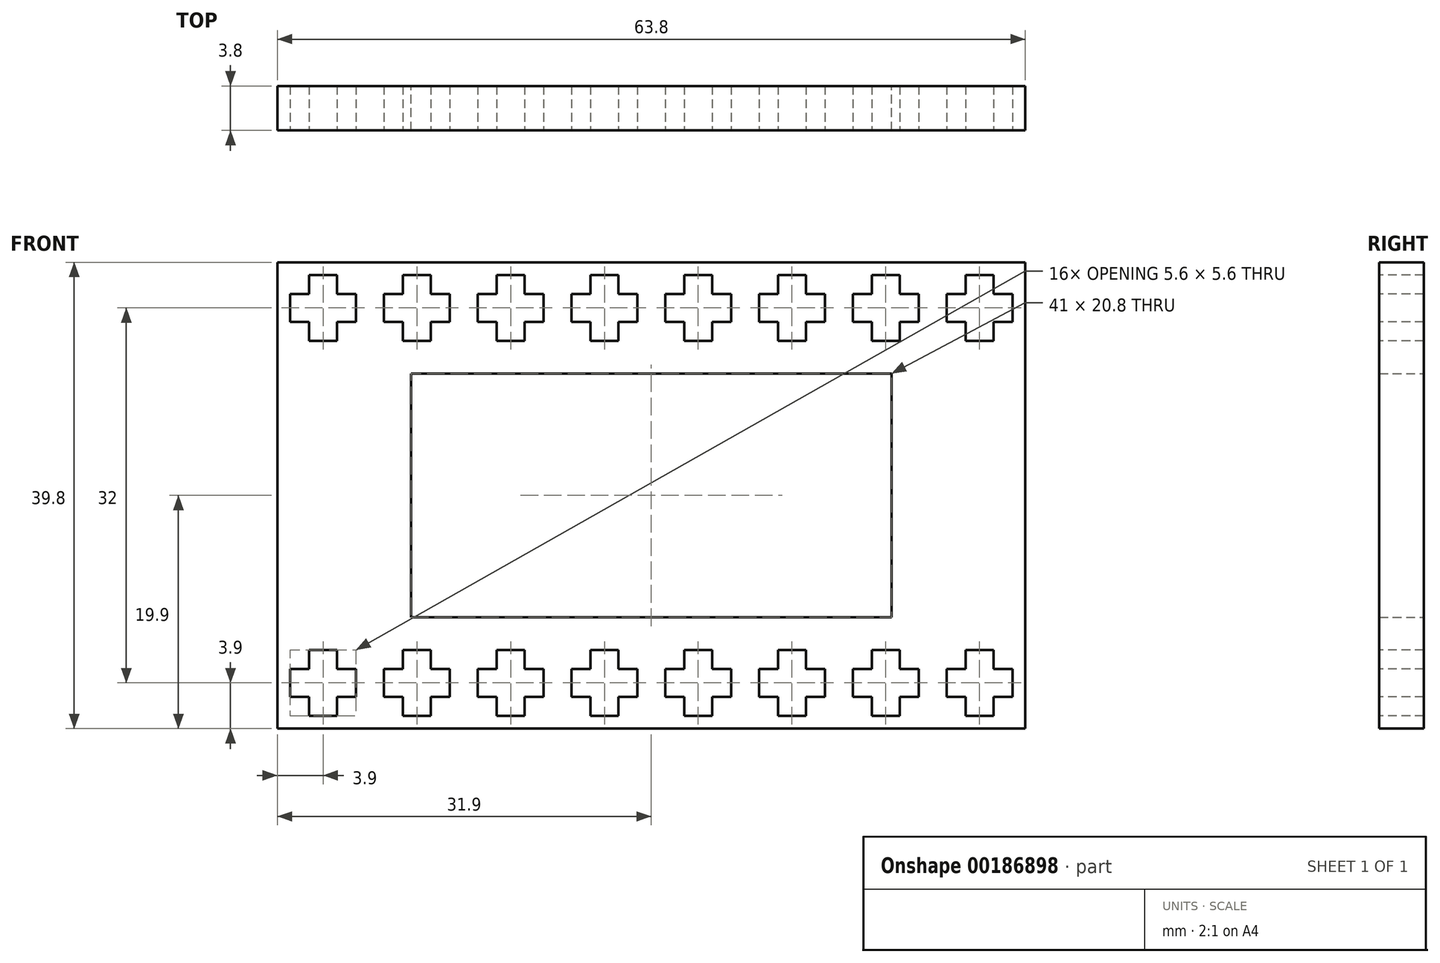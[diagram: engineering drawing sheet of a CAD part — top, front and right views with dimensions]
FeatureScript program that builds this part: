
annotation { "Feature Type Name" : "Feature", "Feature Type Description" : "" }
export const myFeature = defineFeature(function(context is Context, id is Id, definition is map)
    precondition{}
    {
        {
            var Q0;
            Q0=qCreatedBy(makeId("Front.planeOp"),FACE);
            var sketch = newSketch(context, id + "F0", { "sketchPlane" : qUnion([Q0])});
            skLineSegment(sketch, "E0.bottom", {"start": v(20.5, 10.4) * mm, "end": v(-20.5, 10.4) * mm});
            skLineSegment(sketch, "E0.top", {"start": v(20.5, -10.4) * mm, "end": v(-20.5, -10.4) * mm});
            skLineSegment(sketch, "E0.left", {"start": v(20.5, 10.4) * mm, "end": v(20.5, -10.4) * mm});
            skLineSegment(sketch, "E0.right", {"start": v(-20.5, 10.4) * mm, "end": v(-20.5, -10.4) * mm});
            skPoint(sketch, "E0.middle", {"position": v(0, 0) * mm});
            skLineSegment(sketch, "E1.bottom", {"start": v(31.9, -19.9) * mm, "end": v(-31.9, -19.9) * mm});
            skLineSegment(sketch, "E1.top", {"start": v(31.9, 19.9) * mm, "end": v(-31.9, 19.9) * mm});
            skLineSegment(sketch, "E1.left", {"start": v(31.9, -19.9) * mm, "end": v(31.9, 19.9) * mm});
            skLineSegment(sketch, "E1.right", {"start": v(-31.9, -19.9) * mm, "end": v(-31.9, 19.9) * mm});
            skSolve(sketch);
        }
        {
            var Q0;
            Q0 = qSketchRegion(id + "F0", true);
            extrude(context, id + "F1", {"entities" : qUnion([Q0]), "depth" : 3.8 * mm});
        }
        {
            var Q0;
            Q0=makeQuery(id+"F1.opExtrude","CAP_FACE",FACE,{"disambiguationData":[OSD([sQuery(id+"F0.wireOp",EDGE,"E0.bottom"),sQuery(id+"F0.wireOp",EDGE,"E0.top"),sQuery(id+"F0.wireOp",EDGE,"E0.left"),sQuery(id+"F0.wireOp",EDGE,"E0.right"),sQuery(id+"F0.wireOp",EDGE,"E1.bottom"),sQuery(id+"F0.wireOp",EDGE,"E1.top"),sQuery(id+"F0.wireOp",EDGE,"E1.left"),sQuery(id+"F0.wireOp",EDGE,"E1.right")])],"isStart":false});
            var sketch = newSketch(context, id + "F2", { "sketchPlane" : qUnion([Q0])});
            skLineSegment(sketch, "E2", {"start": v(-30.8, 17.2) * mm, "end": v(-29.2, 17.2) * mm});
            skLineSegment(sketch, "E3", {"start": v(-29.2, 17.2) * mm, "end": v(-29.2, 18.8) * mm});
            skLineSegment(sketch, "E4", {"start": v(-29.2, 18.8) * mm, "end": v(-26.8, 18.8) * mm});
            skLineSegment(sketch, "E5", {"start": v(-26.8, 18.8) * mm, "end": v(-26.8, 17.2) * mm});
            skLineSegment(sketch, "E6", {"start": v(-26.8, 17.2) * mm, "end": v(-25.2, 17.2) * mm});
            skLineSegment(sketch, "E7", {"start": v(-25.2, 17.2) * mm, "end": v(-25.2, 14.8) * mm});
            skLineSegment(sketch, "E8", {"start": v(-25.2, 14.8) * mm, "end": v(-26.8, 14.8) * mm});
            skLineSegment(sketch, "E9", {"start": v(-26.8, 14.8) * mm, "end": v(-26.8, 13.2) * mm});
            skLineSegment(sketch, "E10", {"start": v(-26.8, 13.2) * mm, "end": v(-29.2, 13.2) * mm});
            skLineSegment(sketch, "E11", {"start": v(-29.2, 13.2) * mm, "end": v(-29.2, 14.8) * mm});
            skLineSegment(sketch, "E12", {"start": v(-30.8, 17.2) * mm, "end": v(-30.8, 14.8) * mm});
            skLineSegment(sketch, "E13", {"start": v(-30.8, 14.8) * mm, "end": v(-29.2, 14.8) * mm});
            skPoint(sketch, "E14", {"position": v(-30.8, 16) * mm});
            skPoint(sketch, "E15", {"position": v(-28, 18.8) * mm});
            skLineSegment(sketch, "E16.0.1.0", {"start": v(-29.2, -13.2) * mm, "end": v(-26.8, -13.2) * mm});
            skLineSegment(sketch, "E16.0.1.1", {"start": v(-26.8, -13.2) * mm, "end": v(-26.8, -14.8) * mm});
            skLineSegment(sketch, "E16.0.1.2", {"start": v(-26.8, -14.8) * mm, "end": v(-25.2, -14.8) * mm});
            skLineSegment(sketch, "E16.0.1.3", {"start": v(-25.2, -14.8) * mm, "end": v(-25.2, -17.2) * mm});
            skLineSegment(sketch, "E16.0.1.4", {"start": v(-25.2, -17.2) * mm, "end": v(-26.8, -17.2) * mm});
            skLineSegment(sketch, "E16.0.1.5", {"start": v(-26.8, -17.2) * mm, "end": v(-26.8, -18.8) * mm});
            skLineSegment(sketch, "E16.0.1.6", {"start": v(-29.2, -18.8) * mm, "end": v(-29.2, -17.2) * mm});
            skLineSegment(sketch, "E16.0.1.7", {"start": v(-30.8, -17.2) * mm, "end": v(-29.2, -17.2) * mm});
            skLineSegment(sketch, "E16.0.1.8", {"start": v(-30.8, -14.8) * mm, "end": v(-30.8, -17.2) * mm});
            skLineSegment(sketch, "E16.0.1.9", {"start": v(-30.8, -14.8) * mm, "end": v(-29.2, -14.8) * mm});
            skLineSegment(sketch, "E16.0.1.10", {"start": v(-29.2, -14.8) * mm, "end": v(-29.2, -13.2) * mm});
            skLineSegment(sketch, "E16.0.1.11", {"start": v(-26.8, -18.8) * mm, "end": v(-29.2, -18.8) * mm});
            skLineSegment(sketch, "E16.1.0.0", {"start": v(-21.2, 18.8) * mm, "end": v(-18.8, 18.8) * mm});
            skLineSegment(sketch, "E16.1.0.1", {"start": v(-18.8, 18.8) * mm, "end": v(-18.8, 17.2) * mm});
            skLineSegment(sketch, "E16.1.0.2", {"start": v(-18.8, 17.2) * mm, "end": v(-17.2, 17.2) * mm});
            skLineSegment(sketch, "E16.1.0.3", {"start": v(-17.2, 17.2) * mm, "end": v(-17.2, 14.8) * mm});
            skLineSegment(sketch, "E16.1.0.4", {"start": v(-17.2, 14.8) * mm, "end": v(-18.8, 14.8) * mm});
            skLineSegment(sketch, "E16.1.0.5", {"start": v(-18.8, 14.8) * mm, "end": v(-18.8, 13.2) * mm});
            skLineSegment(sketch, "E16.1.0.6", {"start": v(-21.2, 13.2) * mm, "end": v(-21.2, 14.8) * mm});
            skLineSegment(sketch, "E16.1.0.7", {"start": v(-22.8, 14.8) * mm, "end": v(-21.2, 14.8) * mm});
            skLineSegment(sketch, "E16.1.0.8", {"start": v(-22.8, 17.2) * mm, "end": v(-22.8, 14.8) * mm});
            skLineSegment(sketch, "E16.1.0.9", {"start": v(-22.8, 17.2) * mm, "end": v(-21.2, 17.2) * mm});
            skLineSegment(sketch, "E16.1.0.10", {"start": v(-21.2, 17.2) * mm, "end": v(-21.2, 18.8) * mm});
            skLineSegment(sketch, "E16.1.0.11", {"start": v(-18.8, 13.2) * mm, "end": v(-21.2, 13.2) * mm});
            skLineSegment(sketch, "E16.1.1.0", {"start": v(-21.2, -13.2) * mm, "end": v(-18.8, -13.2) * mm});
            skLineSegment(sketch, "E16.1.1.1", {"start": v(-18.8, -13.2) * mm, "end": v(-18.8, -14.8) * mm});
            skLineSegment(sketch, "E16.1.1.2", {"start": v(-18.8, -14.8) * mm, "end": v(-17.2, -14.8) * mm});
            skLineSegment(sketch, "E16.1.1.3", {"start": v(-17.2, -14.8) * mm, "end": v(-17.2, -17.2) * mm});
            skLineSegment(sketch, "E16.1.1.4", {"start": v(-17.2, -17.2) * mm, "end": v(-18.8, -17.2) * mm});
            skLineSegment(sketch, "E16.1.1.5", {"start": v(-18.8, -17.2) * mm, "end": v(-18.8, -18.8) * mm});
            skLineSegment(sketch, "E16.1.1.6", {"start": v(-21.2, -18.8) * mm, "end": v(-21.2, -17.2) * mm});
            skLineSegment(sketch, "E16.1.1.7", {"start": v(-22.8, -17.2) * mm, "end": v(-21.2, -17.2) * mm});
            skLineSegment(sketch, "E16.1.1.8", {"start": v(-22.8, -14.8) * mm, "end": v(-22.8, -17.2) * mm});
            skLineSegment(sketch, "E16.1.1.9", {"start": v(-22.8, -14.8) * mm, "end": v(-21.2, -14.8) * mm});
            skLineSegment(sketch, "E16.1.1.10", {"start": v(-21.2, -14.8) * mm, "end": v(-21.2, -13.2) * mm});
            skLineSegment(sketch, "E16.1.1.11", {"start": v(-18.8, -18.8) * mm, "end": v(-21.2, -18.8) * mm});
            skLineSegment(sketch, "E16.2.0.0", {"start": v(-13.2, 18.8) * mm, "end": v(-10.8, 18.8) * mm});
            skLineSegment(sketch, "E16.2.0.1", {"start": v(-10.8, 18.8) * mm, "end": v(-10.8, 17.2) * mm});
            skLineSegment(sketch, "E16.2.0.2", {"start": v(-10.8, 17.2) * mm, "end": v(-9.2, 17.2) * mm});
            skLineSegment(sketch, "E16.2.0.3", {"start": v(-9.2, 17.2) * mm, "end": v(-9.2, 14.8) * mm});
            skLineSegment(sketch, "E16.2.0.4", {"start": v(-9.2, 14.8) * mm, "end": v(-10.8, 14.8) * mm});
            skLineSegment(sketch, "E16.2.0.5", {"start": v(-10.8, 14.8) * mm, "end": v(-10.8, 13.2) * mm});
            skLineSegment(sketch, "E16.2.0.6", {"start": v(-13.2, 13.2) * mm, "end": v(-13.2, 14.8) * mm});
            skLineSegment(sketch, "E16.2.0.7", {"start": v(-14.8, 14.8) * mm, "end": v(-13.2, 14.8) * mm});
            skLineSegment(sketch, "E16.2.0.8", {"start": v(-14.8, 17.2) * mm, "end": v(-14.8, 14.8) * mm});
            skLineSegment(sketch, "E16.2.0.9", {"start": v(-14.8, 17.2) * mm, "end": v(-13.2, 17.2) * mm});
            skLineSegment(sketch, "E16.2.0.10", {"start": v(-13.2, 17.2) * mm, "end": v(-13.2, 18.8) * mm});
            skLineSegment(sketch, "E16.2.0.11", {"start": v(-10.8, 13.2) * mm, "end": v(-13.2, 13.2) * mm});
            skLineSegment(sketch, "E16.2.1.0", {"start": v(-13.2, -13.2) * mm, "end": v(-10.8, -13.2) * mm});
            skLineSegment(sketch, "E16.2.1.1", {"start": v(-10.8, -13.2) * mm, "end": v(-10.8, -14.8) * mm});
            skLineSegment(sketch, "E16.2.1.2", {"start": v(-10.8, -14.8) * mm, "end": v(-9.2, -14.8) * mm});
            skLineSegment(sketch, "E16.2.1.3", {"start": v(-9.2, -14.8) * mm, "end": v(-9.2, -17.2) * mm});
            skLineSegment(sketch, "E16.2.1.4", {"start": v(-9.2, -17.2) * mm, "end": v(-10.8, -17.2) * mm});
            skLineSegment(sketch, "E16.2.1.5", {"start": v(-10.8, -17.2) * mm, "end": v(-10.8, -18.8) * mm});
            skLineSegment(sketch, "E16.2.1.6", {"start": v(-13.2, -18.8) * mm, "end": v(-13.2, -17.2) * mm});
            skLineSegment(sketch, "E16.2.1.7", {"start": v(-14.8, -17.2) * mm, "end": v(-13.2, -17.2) * mm});
            skLineSegment(sketch, "E16.2.1.8", {"start": v(-14.8, -14.8) * mm, "end": v(-14.8, -17.2) * mm});
            skLineSegment(sketch, "E16.2.1.9", {"start": v(-14.8, -14.8) * mm, "end": v(-13.2, -14.8) * mm});
            skLineSegment(sketch, "E16.2.1.10", {"start": v(-13.2, -14.8) * mm, "end": v(-13.2, -13.2) * mm});
            skLineSegment(sketch, "E16.2.1.11", {"start": v(-10.8, -18.8) * mm, "end": v(-13.2, -18.8) * mm});
            skLineSegment(sketch, "E16.3.0.0", {"start": v(-5.2, 18.8) * mm, "end": v(-2.8, 18.8) * mm});
            skLineSegment(sketch, "E16.3.0.1", {"start": v(-2.8, 18.8) * mm, "end": v(-2.8, 17.2) * mm});
            skLineSegment(sketch, "E16.3.0.2", {"start": v(-2.8, 17.2) * mm, "end": v(-1.2, 17.2) * mm});
            skLineSegment(sketch, "E16.3.0.3", {"start": v(-1.2, 17.2) * mm, "end": v(-1.2, 14.8) * mm});
            skLineSegment(sketch, "E16.3.0.4", {"start": v(-1.2, 14.8) * mm, "end": v(-2.8, 14.8) * mm});
            skLineSegment(sketch, "E16.3.0.5", {"start": v(-2.8, 14.8) * mm, "end": v(-2.8, 13.2) * mm});
            skLineSegment(sketch, "E16.3.0.6", {"start": v(-5.2, 13.2) * mm, "end": v(-5.2, 14.8) * mm});
            skLineSegment(sketch, "E16.3.0.7", {"start": v(-6.8, 14.8) * mm, "end": v(-5.2, 14.8) * mm});
            skLineSegment(sketch, "E16.3.0.8", {"start": v(-6.8, 17.2) * mm, "end": v(-6.8, 14.8) * mm});
            skLineSegment(sketch, "E16.3.0.9", {"start": v(-6.8, 17.2) * mm, "end": v(-5.2, 17.2) * mm});
            skLineSegment(sketch, "E16.3.0.10", {"start": v(-5.2, 17.2) * mm, "end": v(-5.2, 18.8) * mm});
            skLineSegment(sketch, "E16.3.0.11", {"start": v(-2.8, 13.2) * mm, "end": v(-5.2, 13.2) * mm});
            skLineSegment(sketch, "E16.3.1.0", {"start": v(-5.2, -13.2) * mm, "end": v(-2.8, -13.2) * mm});
            skLineSegment(sketch, "E16.3.1.1", {"start": v(-2.8, -13.2) * mm, "end": v(-2.8, -14.8) * mm});
            skLineSegment(sketch, "E16.3.1.2", {"start": v(-2.8, -14.8) * mm, "end": v(-1.2, -14.8) * mm});
            skLineSegment(sketch, "E16.3.1.3", {"start": v(-1.2, -14.8) * mm, "end": v(-1.2, -17.2) * mm});
            skLineSegment(sketch, "E16.3.1.4", {"start": v(-1.2, -17.2) * mm, "end": v(-2.8, -17.2) * mm});
            skLineSegment(sketch, "E16.3.1.5", {"start": v(-2.8, -17.2) * mm, "end": v(-2.8, -18.8) * mm});
            skLineSegment(sketch, "E16.3.1.6", {"start": v(-5.2, -18.8) * mm, "end": v(-5.2, -17.2) * mm});
            skLineSegment(sketch, "E16.3.1.7", {"start": v(-6.8, -17.2) * mm, "end": v(-5.2, -17.2) * mm});
            skLineSegment(sketch, "E16.3.1.8", {"start": v(-6.8, -14.8) * mm, "end": v(-6.8, -17.2) * mm});
            skLineSegment(sketch, "E16.3.1.9", {"start": v(-6.8, -14.8) * mm, "end": v(-5.2, -14.8) * mm});
            skLineSegment(sketch, "E16.3.1.10", {"start": v(-5.2, -14.8) * mm, "end": v(-5.2, -13.2) * mm});
            skLineSegment(sketch, "E16.3.1.11", {"start": v(-2.8, -18.8) * mm, "end": v(-5.2, -18.8) * mm});
            skLineSegment(sketch, "E16.4.0.0", {"start": v(2.8, 18.8) * mm, "end": v(5.2, 18.8) * mm});
            skLineSegment(sketch, "E16.4.0.1", {"start": v(5.2, 18.8) * mm, "end": v(5.2, 17.2) * mm});
            skLineSegment(sketch, "E16.4.0.2", {"start": v(5.2, 17.2) * mm, "end": v(6.8, 17.2) * mm});
            skLineSegment(sketch, "E16.4.0.3", {"start": v(6.8, 17.2) * mm, "end": v(6.8, 14.8) * mm});
            skLineSegment(sketch, "E16.4.0.4", {"start": v(6.8, 14.8) * mm, "end": v(5.2, 14.8) * mm});
            skLineSegment(sketch, "E16.4.0.5", {"start": v(5.2, 14.8) * mm, "end": v(5.2, 13.2) * mm});
            skLineSegment(sketch, "E16.4.0.6", {"start": v(2.8, 13.2) * mm, "end": v(2.8, 14.8) * mm});
            skLineSegment(sketch, "E16.4.0.7", {"start": v(1.2, 14.8) * mm, "end": v(2.8, 14.8) * mm});
            skLineSegment(sketch, "E16.4.0.8", {"start": v(1.2, 17.2) * mm, "end": v(1.2, 14.8) * mm});
            skLineSegment(sketch, "E16.4.0.9", {"start": v(1.2, 17.2) * mm, "end": v(2.8, 17.2) * mm});
            skLineSegment(sketch, "E16.4.0.10", {"start": v(2.8, 17.2) * mm, "end": v(2.8, 18.8) * mm});
            skLineSegment(sketch, "E16.4.0.11", {"start": v(5.2, 13.2) * mm, "end": v(2.8, 13.2) * mm});
            skLineSegment(sketch, "E16.4.1.0", {"start": v(2.8, -13.2) * mm, "end": v(5.2, -13.2) * mm});
            skLineSegment(sketch, "E16.4.1.1", {"start": v(5.2, -13.2) * mm, "end": v(5.2, -14.8) * mm});
            skLineSegment(sketch, "E16.4.1.2", {"start": v(5.2, -14.8) * mm, "end": v(6.8, -14.8) * mm});
            skLineSegment(sketch, "E16.4.1.3", {"start": v(6.8, -14.8) * mm, "end": v(6.8, -17.2) * mm});
            skLineSegment(sketch, "E16.4.1.4", {"start": v(6.8, -17.2) * mm, "end": v(5.2, -17.2) * mm});
            skLineSegment(sketch, "E16.4.1.5", {"start": v(5.2, -17.2) * mm, "end": v(5.2, -18.8) * mm});
            skLineSegment(sketch, "E16.4.1.6", {"start": v(2.8, -18.8) * mm, "end": v(2.8, -17.2) * mm});
            skLineSegment(sketch, "E16.4.1.7", {"start": v(1.2, -17.2) * mm, "end": v(2.8, -17.2) * mm});
            skLineSegment(sketch, "E16.4.1.8", {"start": v(1.2, -14.8) * mm, "end": v(1.2, -17.2) * mm});
            skLineSegment(sketch, "E16.4.1.9", {"start": v(1.2, -14.8) * mm, "end": v(2.8, -14.8) * mm});
            skLineSegment(sketch, "E16.4.1.10", {"start": v(2.8, -14.8) * mm, "end": v(2.8, -13.2) * mm});
            skLineSegment(sketch, "E16.4.1.11", {"start": v(5.2, -18.8) * mm, "end": v(2.8, -18.8) * mm});
            skLineSegment(sketch, "E16.5.0.0", {"start": v(10.8, 18.8) * mm, "end": v(13.2, 18.8) * mm});
            skLineSegment(sketch, "E16.5.0.1", {"start": v(13.2, 18.8) * mm, "end": v(13.2, 17.2) * mm});
            skLineSegment(sketch, "E16.5.0.2", {"start": v(13.2, 17.2) * mm, "end": v(14.8, 17.2) * mm});
            skLineSegment(sketch, "E16.5.0.3", {"start": v(14.8, 17.2) * mm, "end": v(14.8, 14.8) * mm});
            skLineSegment(sketch, "E16.5.0.4", {"start": v(14.8, 14.8) * mm, "end": v(13.2, 14.8) * mm});
            skLineSegment(sketch, "E16.5.0.5", {"start": v(13.2, 14.8) * mm, "end": v(13.2, 13.2) * mm});
            skLineSegment(sketch, "E16.5.0.6", {"start": v(10.8, 13.2) * mm, "end": v(10.8, 14.8) * mm});
            skLineSegment(sketch, "E16.5.0.7", {"start": v(9.2, 14.8) * mm, "end": v(10.8, 14.8) * mm});
            skLineSegment(sketch, "E16.5.0.8", {"start": v(9.2, 17.2) * mm, "end": v(9.2, 14.8) * mm});
            skLineSegment(sketch, "E16.5.0.9", {"start": v(9.2, 17.2) * mm, "end": v(10.8, 17.2) * mm});
            skLineSegment(sketch, "E16.5.0.10", {"start": v(10.8, 17.2) * mm, "end": v(10.8, 18.8) * mm});
            skLineSegment(sketch, "E16.5.0.11", {"start": v(13.2, 13.2) * mm, "end": v(10.8, 13.2) * mm});
            skLineSegment(sketch, "E16.5.1.0", {"start": v(10.8, -13.2) * mm, "end": v(13.2, -13.2) * mm});
            skLineSegment(sketch, "E16.5.1.1", {"start": v(13.2, -13.2) * mm, "end": v(13.2, -14.8) * mm});
            skLineSegment(sketch, "E16.5.1.2", {"start": v(13.2, -14.8) * mm, "end": v(14.8, -14.8) * mm});
            skLineSegment(sketch, "E16.5.1.3", {"start": v(14.8, -14.8) * mm, "end": v(14.8, -17.2) * mm});
            skLineSegment(sketch, "E16.5.1.4", {"start": v(14.8, -17.2) * mm, "end": v(13.2, -17.2) * mm});
            skLineSegment(sketch, "E16.5.1.5", {"start": v(13.2, -17.2) * mm, "end": v(13.2, -18.8) * mm});
            skLineSegment(sketch, "E16.5.1.6", {"start": v(10.8, -18.8) * mm, "end": v(10.8, -17.2) * mm});
            skLineSegment(sketch, "E16.5.1.7", {"start": v(9.2, -17.2) * mm, "end": v(10.8, -17.2) * mm});
            skLineSegment(sketch, "E16.5.1.8", {"start": v(9.2, -14.8) * mm, "end": v(9.2, -17.2) * mm});
            skLineSegment(sketch, "E16.5.1.9", {"start": v(9.2, -14.8) * mm, "end": v(10.8, -14.8) * mm});
            skLineSegment(sketch, "E16.5.1.10", {"start": v(10.8, -14.8) * mm, "end": v(10.8, -13.2) * mm});
            skLineSegment(sketch, "E16.5.1.11", {"start": v(13.2, -18.8) * mm, "end": v(10.8, -18.8) * mm});
            skLineSegment(sketch, "E16.6.0.0", {"start": v(18.8, 18.8) * mm, "end": v(21.2, 18.8) * mm});
            skLineSegment(sketch, "E16.6.0.1", {"start": v(21.2, 18.8) * mm, "end": v(21.2, 17.2) * mm});
            skLineSegment(sketch, "E16.6.0.2", {"start": v(21.2, 17.2) * mm, "end": v(22.8, 17.2) * mm});
            skLineSegment(sketch, "E16.6.0.3", {"start": v(22.8, 17.2) * mm, "end": v(22.8, 14.8) * mm});
            skLineSegment(sketch, "E16.6.0.4", {"start": v(22.8, 14.8) * mm, "end": v(21.2, 14.8) * mm});
            skLineSegment(sketch, "E16.6.0.5", {"start": v(21.2, 14.8) * mm, "end": v(21.2, 13.2) * mm});
            skLineSegment(sketch, "E16.6.0.6", {"start": v(18.8, 13.2) * mm, "end": v(18.8, 14.8) * mm});
            skLineSegment(sketch, "E16.6.0.7", {"start": v(17.2, 14.8) * mm, "end": v(18.8, 14.8) * mm});
            skLineSegment(sketch, "E16.6.0.8", {"start": v(17.2, 17.2) * mm, "end": v(17.2, 14.8) * mm});
            skLineSegment(sketch, "E16.6.0.9", {"start": v(17.2, 17.2) * mm, "end": v(18.8, 17.2) * mm});
            skLineSegment(sketch, "E16.6.0.10", {"start": v(18.8, 17.2) * mm, "end": v(18.8, 18.8) * mm});
            skLineSegment(sketch, "E16.6.0.11", {"start": v(21.2, 13.2) * mm, "end": v(18.8, 13.2) * mm});
            skLineSegment(sketch, "E16.6.1.0", {"start": v(18.8, -13.2) * mm, "end": v(21.2, -13.2) * mm});
            skLineSegment(sketch, "E16.6.1.1", {"start": v(21.2, -13.2) * mm, "end": v(21.2, -14.8) * mm});
            skLineSegment(sketch, "E16.6.1.2", {"start": v(21.2, -14.8) * mm, "end": v(22.8, -14.8) * mm});
            skLineSegment(sketch, "E16.6.1.3", {"start": v(22.8, -14.8) * mm, "end": v(22.8, -17.2) * mm});
            skLineSegment(sketch, "E16.6.1.4", {"start": v(22.8, -17.2) * mm, "end": v(21.2, -17.2) * mm});
            skLineSegment(sketch, "E16.6.1.5", {"start": v(21.2, -17.2) * mm, "end": v(21.2, -18.8) * mm});
            skLineSegment(sketch, "E16.6.1.6", {"start": v(18.8, -18.8) * mm, "end": v(18.8, -17.2) * mm});
            skLineSegment(sketch, "E16.6.1.7", {"start": v(17.2, -17.2) * mm, "end": v(18.8, -17.2) * mm});
            skLineSegment(sketch, "E16.6.1.8", {"start": v(17.2, -14.8) * mm, "end": v(17.2, -17.2) * mm});
            skLineSegment(sketch, "E16.6.1.9", {"start": v(17.2, -14.8) * mm, "end": v(18.8, -14.8) * mm});
            skLineSegment(sketch, "E16.6.1.10", {"start": v(18.8, -14.8) * mm, "end": v(18.8, -13.2) * mm});
            skLineSegment(sketch, "E16.6.1.11", {"start": v(21.2, -18.8) * mm, "end": v(18.8, -18.8) * mm});
            skLineSegment(sketch, "E16.7.0.0", {"start": v(26.8, 18.8) * mm, "end": v(29.2, 18.8) * mm});
            skLineSegment(sketch, "E16.7.0.1", {"start": v(29.2, 18.8) * mm, "end": v(29.2, 17.2) * mm});
            skLineSegment(sketch, "E16.7.0.2", {"start": v(29.2, 17.2) * mm, "end": v(30.8, 17.2) * mm});
            skLineSegment(sketch, "E16.7.0.3", {"start": v(30.8, 17.2) * mm, "end": v(30.8, 14.8) * mm});
            skLineSegment(sketch, "E16.7.0.4", {"start": v(30.8, 14.8) * mm, "end": v(29.2, 14.8) * mm});
            skLineSegment(sketch, "E16.7.0.5", {"start": v(29.2, 14.8) * mm, "end": v(29.2, 13.2) * mm});
            skLineSegment(sketch, "E16.7.0.6", {"start": v(26.8, 13.2) * mm, "end": v(26.8, 14.8) * mm});
            skLineSegment(sketch, "E16.7.0.7", {"start": v(25.2, 14.8) * mm, "end": v(26.8, 14.8) * mm});
            skLineSegment(sketch, "E16.7.0.8", {"start": v(25.2, 17.2) * mm, "end": v(25.2, 14.8) * mm});
            skLineSegment(sketch, "E16.7.0.9", {"start": v(25.2, 17.2) * mm, "end": v(26.8, 17.2) * mm});
            skLineSegment(sketch, "E16.7.0.10", {"start": v(26.8, 17.2) * mm, "end": v(26.8, 18.8) * mm});
            skLineSegment(sketch, "E16.7.0.11", {"start": v(29.2, 13.2) * mm, "end": v(26.8, 13.2) * mm});
            skLineSegment(sketch, "E16.7.1.0", {"start": v(26.8, -13.2) * mm, "end": v(29.2, -13.2) * mm});
            skLineSegment(sketch, "E16.7.1.1", {"start": v(29.2, -13.2) * mm, "end": v(29.2, -14.8) * mm});
            skLineSegment(sketch, "E16.7.1.2", {"start": v(29.2, -14.8) * mm, "end": v(30.8, -14.8) * mm});
            skLineSegment(sketch, "E16.7.1.3", {"start": v(30.8, -14.8) * mm, "end": v(30.8, -17.2) * mm});
            skLineSegment(sketch, "E16.7.1.4", {"start": v(30.8, -17.2) * mm, "end": v(29.2, -17.2) * mm});
            skLineSegment(sketch, "E16.7.1.5", {"start": v(29.2, -17.2) * mm, "end": v(29.2, -18.8) * mm});
            skLineSegment(sketch, "E16.7.1.6", {"start": v(26.8, -18.8) * mm, "end": v(26.8, -17.2) * mm});
            skLineSegment(sketch, "E16.7.1.7", {"start": v(25.2, -17.2) * mm, "end": v(26.8, -17.2) * mm});
            skLineSegment(sketch, "E16.7.1.8", {"start": v(25.2, -14.8) * mm, "end": v(25.2, -17.2) * mm});
            skLineSegment(sketch, "E16.7.1.9", {"start": v(25.2, -14.8) * mm, "end": v(26.8, -14.8) * mm});
            skLineSegment(sketch, "E16.7.1.10", {"start": v(26.8, -14.8) * mm, "end": v(26.8, -13.2) * mm});
            skLineSegment(sketch, "E16.7.1.11", {"start": v(29.2, -18.8) * mm, "end": v(26.8, -18.8) * mm});
            skLineSegment(sketch, "E16.direction1", {"start": v(-29.2, 18.8) * mm, "end": v(-21.2, 18.8) * mm, "construction": true});
            skLineSegment(sketch, "E16.direction2", {"start": v(-29.2, 18.8) * mm, "end": v(-29.2, -13.2) * mm, "construction": true});
            skSolve(sketch);
        }
        {
            var Q0;
            Q0 = qSketchRegion(id + "F2", true);
            extrude(context, id + "F3", {"entities" : qUnion([Q0]), "operationType" : NewBodyOperationType.REMOVE, "oppositeDirection" : true, "depth" : 25 * mm});
        }
    });
